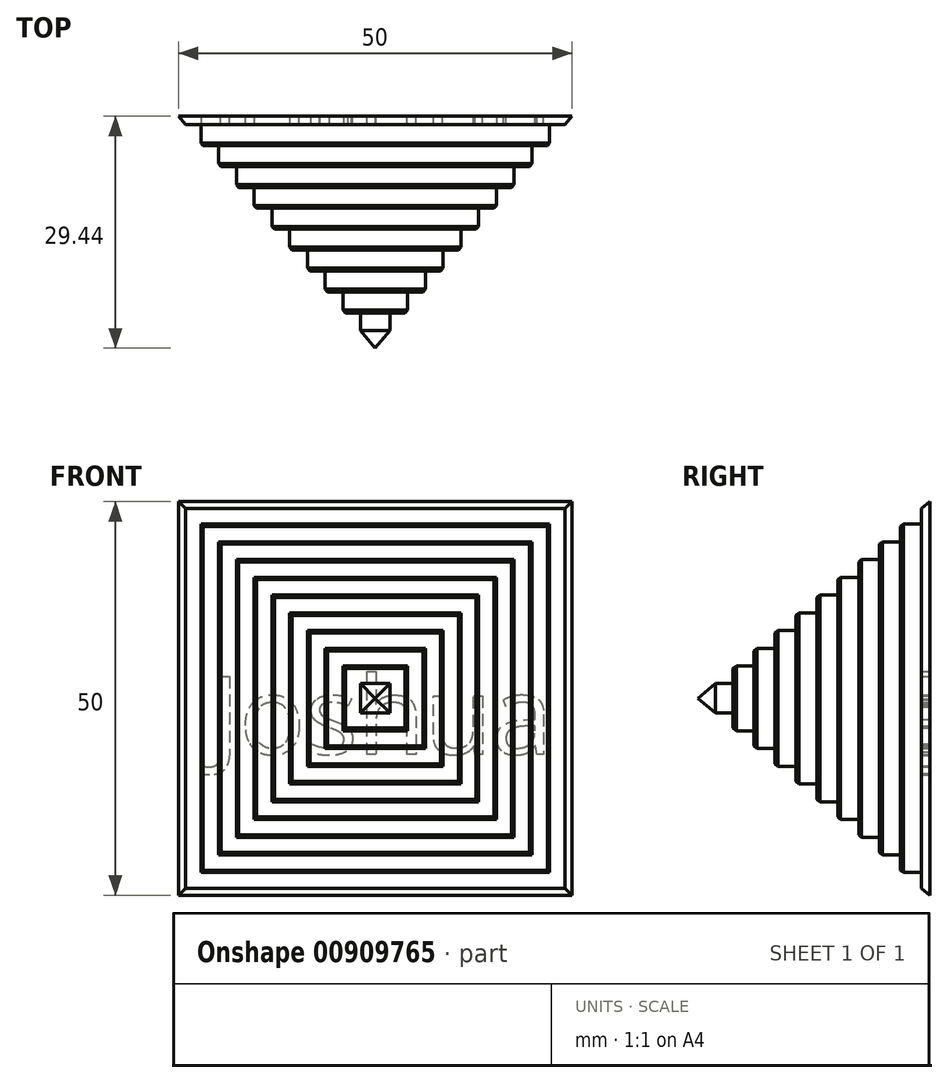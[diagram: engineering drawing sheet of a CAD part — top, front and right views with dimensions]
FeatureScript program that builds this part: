
annotation { "Feature Type Name" : "Feature", "Feature Type Description" : "" }
export const myFeature = defineFeature(function(context is Context, id is Id, definition is map)
    precondition{}
    {
        {
            var Q0;
            Q0=qCreatedBy(makeId("Front.planeOp"),FACE);
            var sketch = newSketch(context, id + "F0", { "sketchPlane" : qUnion([Q0])});
            skLineSegment(sketch, "E0.bottom", {"start": v(25, 25) * mm, "end": v(-25, 25) * mm});
            skLineSegment(sketch, "E0.top", {"start": v(25, -25) * mm, "end": v(-25, -25) * mm});
            skLineSegment(sketch, "E0.left", {"start": v(25, 25) * mm, "end": v(25, -25) * mm});
            skLineSegment(sketch, "E0.right", {"start": v(-25, 25) * mm, "end": v(-25, -25) * mm});
            skPoint(sketch, "E0.middle", {"position": v(0, 0) * mm});
            skSolve(sketch);
        }
        {
            var Q0;
            Q0=qCreatedBy(makeId("Top.planeOp"),FACE);
            var sketch = newSketch(context, id + "F1", { "sketchPlane" : qUnion([Q0])});
            skLineSegment(sketch, "E1", {"start": v(0, 0) * mm, "end": v(0, -29.44) * mm});
            skLineSegment(sketch, "E2", {"start": v(0, -29.44) * mm, "end": v(1.87, -27.24) * mm});
            skLineSegment(sketch, "E3", {"start": v(0, 0) * mm, "end": v(25, 0) * mm});
            skLineSegment(sketch, "E4", {"start": v(22.14, -1.94) * mm, "end": v(22.14, -1.05) * mm});
            skLineSegment(sketch, "E5", {"start": v(22.14, -1.05) * mm, "end": v(24.11, -1.05) * mm});
            skLineSegment(sketch, "E6.0.1.0", {"start": v(19.88, -4.6) * mm, "end": v(19.88, -3.7) * mm});
            skLineSegment(sketch, "E6.0.1.1", {"start": v(19.88, -3.7) * mm, "end": v(21.86, -3.7) * mm});
            skLineSegment(sketch, "E6.0.1.2", {"start": v(21.1, -4.6) * mm, "end": v(21.1, -4.6) * mm});
            skLineSegment(sketch, "E6.0.2.0", {"start": v(17.63, -7.26) * mm, "end": v(17.63, -6.37) * mm});
            skLineSegment(sketch, "E6.0.2.1", {"start": v(17.63, -6.37) * mm, "end": v(19.6, -6.37) * mm});
            skLineSegment(sketch, "E6.0.3.0", {"start": v(15.38, -9.92) * mm, "end": v(15.38, -9.03) * mm});
            skLineSegment(sketch, "E6.0.3.1", {"start": v(15.38, -9.03) * mm, "end": v(17.35, -9.03) * mm});
            skLineSegment(sketch, "E6.0.3.2", {"start": v(16.6, -9.92) * mm, "end": v(16.58, -9.92) * mm});
            skLineSegment(sketch, "E6.0.4.0", {"start": v(13.13, -12.58) * mm, "end": v(13.13, -11.69) * mm});
            skLineSegment(sketch, "E6.0.4.1", {"start": v(13.13, -11.69) * mm, "end": v(15.1, -11.69) * mm});
            skLineSegment(sketch, "E6.0.5.0", {"start": v(10.88, -15.24) * mm, "end": v(10.88, -14.34) * mm});
            skLineSegment(sketch, "E6.0.5.1", {"start": v(10.88, -14.34) * mm, "end": v(12.85, -14.34) * mm});
            skLineSegment(sketch, "E6.0.6.0", {"start": v(8.62, -17.9) * mm, "end": v(8.62, -17) * mm});
            skLineSegment(sketch, "E6.0.6.1", {"start": v(8.62, -17) * mm, "end": v(10.6, -17) * mm});
            skLineSegment(sketch, "E6.0.6.2", {"start": v(9.84, -17.9) * mm, "end": v(9.8, -17.9) * mm});
            skLineSegment(sketch, "E6.0.7.0", {"start": v(6.37, -20.56) * mm, "end": v(6.37, -19.66) * mm});
            skLineSegment(sketch, "E6.0.7.1", {"start": v(6.37, -19.66) * mm, "end": v(8.35, -19.66) * mm});
            skLineSegment(sketch, "E6.0.7.2", {"start": v(7.59, -20.56) * mm, "end": v(7.54, -20.56) * mm});
            skLineSegment(sketch, "E6.0.8.0", {"start": v(4.12, -23.22) * mm, "end": v(4.12, -22.32) * mm});
            skLineSegment(sketch, "E6.0.8.1", {"start": v(4.12, -22.32) * mm, "end": v(6.1, -22.32) * mm});
            skLineSegment(sketch, "E6.0.9.0", {"start": v(1.87, -25.88) * mm, "end": v(1.87, -24.98) * mm});
            skLineSegment(sketch, "E6.0.9.1", {"start": v(1.87, -24.98) * mm, "end": v(3.84, -24.98) * mm});
            skLineSegment(sketch, "E6.0.9.2", {"start": v(3.08, -25.88) * mm, "end": v(3.03, -25.88) * mm});
            skLineSegment(sketch, "E6.direction1", {"start": v(23.35, -1.94) * mm, "end": v(36.62, -1.6) * mm, "construction": true});
            skLineSegment(sketch, "E6.direction2", {"start": v(22.14, -3.38) * mm, "end": v(21.86, -3.7) * mm, "construction": true});
            skLineSegment(sketch, "E7", {"start": v(1.87, -25.88) * mm, "end": v(1.87, -27.24) * mm});
            skLineSegment(sketch, "E8", {"start": v(4.12, -23.22) * mm, "end": v(4.12, -24.59) * mm});
            skLineSegment(sketch, "E9", {"start": v(6.37, -20.56) * mm, "end": v(6.37, -21.93) * mm});
            skLineSegment(sketch, "E10", {"start": v(8.62, -17.9) * mm, "end": v(8.62, -19.28) * mm});
            skLineSegment(sketch, "E11", {"start": v(10.88, -15.24) * mm, "end": v(10.88, -16.63) * mm});
            skLineSegment(sketch, "E12", {"start": v(13.13, -12.58) * mm, "end": v(13.13, -13.98) * mm});
            skLineSegment(sketch, "E13", {"start": v(15.38, -9.92) * mm, "end": v(15.38, -11.33) * mm});
            skLineSegment(sketch, "E14", {"start": v(17.63, -7.26) * mm, "end": v(17.63, -8.68) * mm});
            skLineSegment(sketch, "E15", {"start": v(19.88, -4.6) * mm, "end": v(19.88, -6.02) * mm});
            skLineSegment(sketch, "E16", {"start": v(22.14, -1.94) * mm, "end": v(22.14, -3.38) * mm});
            skLineSegment(sketch, "E17.trimOffspring", {"start": v(3.78, -24.98) * mm, "end": v(4.12, -24.59) * mm});
            skLineSegment(sketch, "E18.trimOffspring", {"start": v(6.04, -22.32) * mm, "end": v(6.37, -21.93) * mm});
            skLineSegment(sketch, "E19.trimOffspring", {"start": v(8.3, -19.66) * mm, "end": v(8.62, -19.28) * mm});
            skLineSegment(sketch, "E20.trimOffspring", {"start": v(10.56, -17) * mm, "end": v(10.88, -16.63) * mm});
            skLineSegment(sketch, "E21.trimOffspring", {"start": v(12.82, -14.34) * mm, "end": v(13.13, -13.98) * mm});
            skLineSegment(sketch, "E22.trimOffspring", {"start": v(15.08, -11.69) * mm, "end": v(15.38, -11.33) * mm});
            skLineSegment(sketch, "E23.trimOffspring", {"start": v(17.34, -9.03) * mm, "end": v(17.63, -8.68) * mm});
            skLineSegment(sketch, "E24.trimOffspring", {"start": v(19.6, -6.37) * mm, "end": v(19.88, -6.02) * mm});
            skLineSegment(sketch, "E25.trimOffspring", {"start": v(21.85, -3.7) * mm, "end": v(22.14, -3.37) * mm});
            skLineSegment(sketch, "E26.trimOffspring", {"start": v(24.11, -1.05) * mm, "end": v(25, 0) * mm});
            skSolve(sketch);
        }
        {
            var Q0;
            Q0=makeQuery(id+"F1.imprint","IMPRINT",FACE,{"disambiguationData":[TD([[makeQuery(id+"F1.imprint","IMPRINT",EDGE,{"derivedFrom":sQuery(id+"F1.wireOp",EDGE,"E1")}),1.0]])]});
            var Q1;
            Q1=sQuery(id+"F0.wireOp",EDGE,"E0.top");
            var Q2;
            Q2=sQuery(id+"F0.wireOp",EDGE,"E0.left");
            var Q3;
            Q3=sQuery(id+"F0.wireOp",EDGE,"E0.right");
            var Q4;
            Q4=sQuery(id+"F0.wireOp",EDGE,"E0.bottom");
            sweep(context, id + "F2", {"profiles" : qUnion([Q0]), "path" : qUnion([Q1, Q2, Q3, Q4])});
        }
        {
            var Q0;
            Q0=makeQuery(id+"F0.imprint","IMPRINT",FACE,{"disambiguationData":[TD([[makeQuery(id+"F0.imprint","IMPRINT",EDGE,{"derivedFrom":sQuery(id+"F0.wireOp",EDGE,"E0.bottom")}),1.0]])]});
            var sketch = newSketch(context, id + "F3", { "sketchPlane" : qUnion([Q0])});
            skText(sketch, "E27", { "text": "Joshua", "fontName": "OpenSans-Regular.ttf"});
            const initialGuessF3  = {"E27": [-0.02097, -0.00713, 1, 0, 0.01]};
            skSetInitialGuess(sketch, initialGuessF3);
            skSolve(sketch);
        }
        {
            var Q0;
            Q0 = qSketchRegion(id + "F3", true);
            extrude(context, id + "F4", {"entities" : qUnion([Q0]), "operationType" : NewBodyOperationType.REMOVE, "depth" : 1 * mm, "offsetDistance" : 25 * mm});
        }
    });
